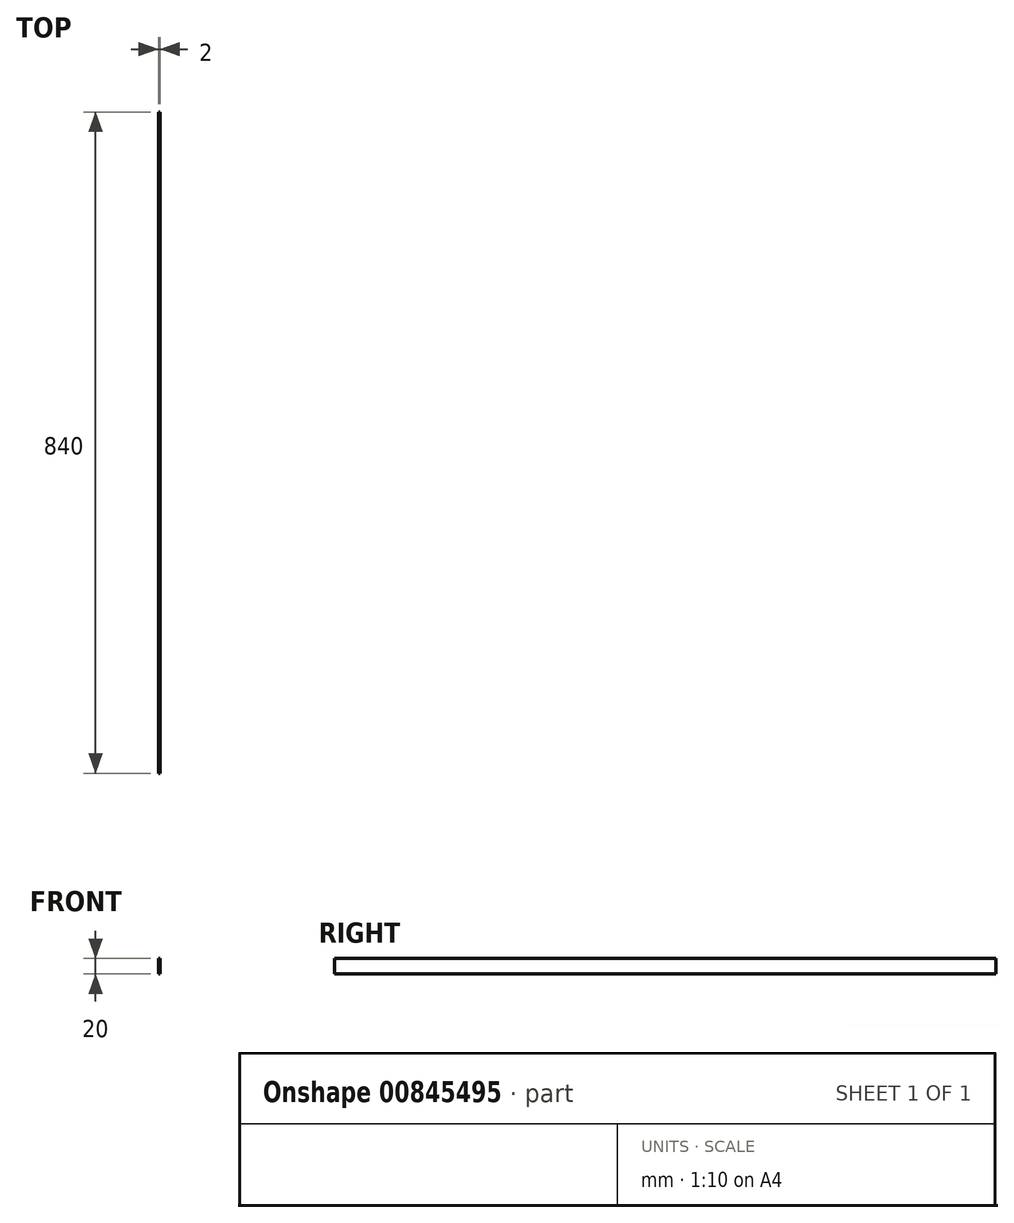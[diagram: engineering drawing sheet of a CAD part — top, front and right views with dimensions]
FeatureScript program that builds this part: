
annotation { "Feature Type Name" : "Feature", "Feature Type Description" : "" }
export const myFeature = defineFeature(function(context is Context, id is Id, definition is map)
    precondition{}
    {
        {
            var Q0;
            Q0=qCreatedBy(makeId("Front.planeOp"),FACE);
            var sketch = newSketch(context, id + "F0", { "sketchPlane" : qUnion([Q0])});
            skLineSegment(sketch, "E0", {"start": v(2, 0) * mm, "end": v(2, 20) * mm});
            skLineSegment(sketch, "E1", {"start": v(2, 20) * mm, "end": v(0, 20) * mm});
            skLineSegment(sketch, "E2", {"start": v(0, 20) * mm, "end": v(0, 0) * mm});
            skLineSegment(sketch, "E3", {"start": v(0, 0) * mm, "end": v(2, 0) * mm});
            skSolve(sketch);
        }
        {
            var Q0;
            Q0=qSketchRegion(id+"F0",true);
            extrude(context, id + "F1", {"entities" : qUnion([Q0]), "depth" : 840 * mm});
        }
    });
